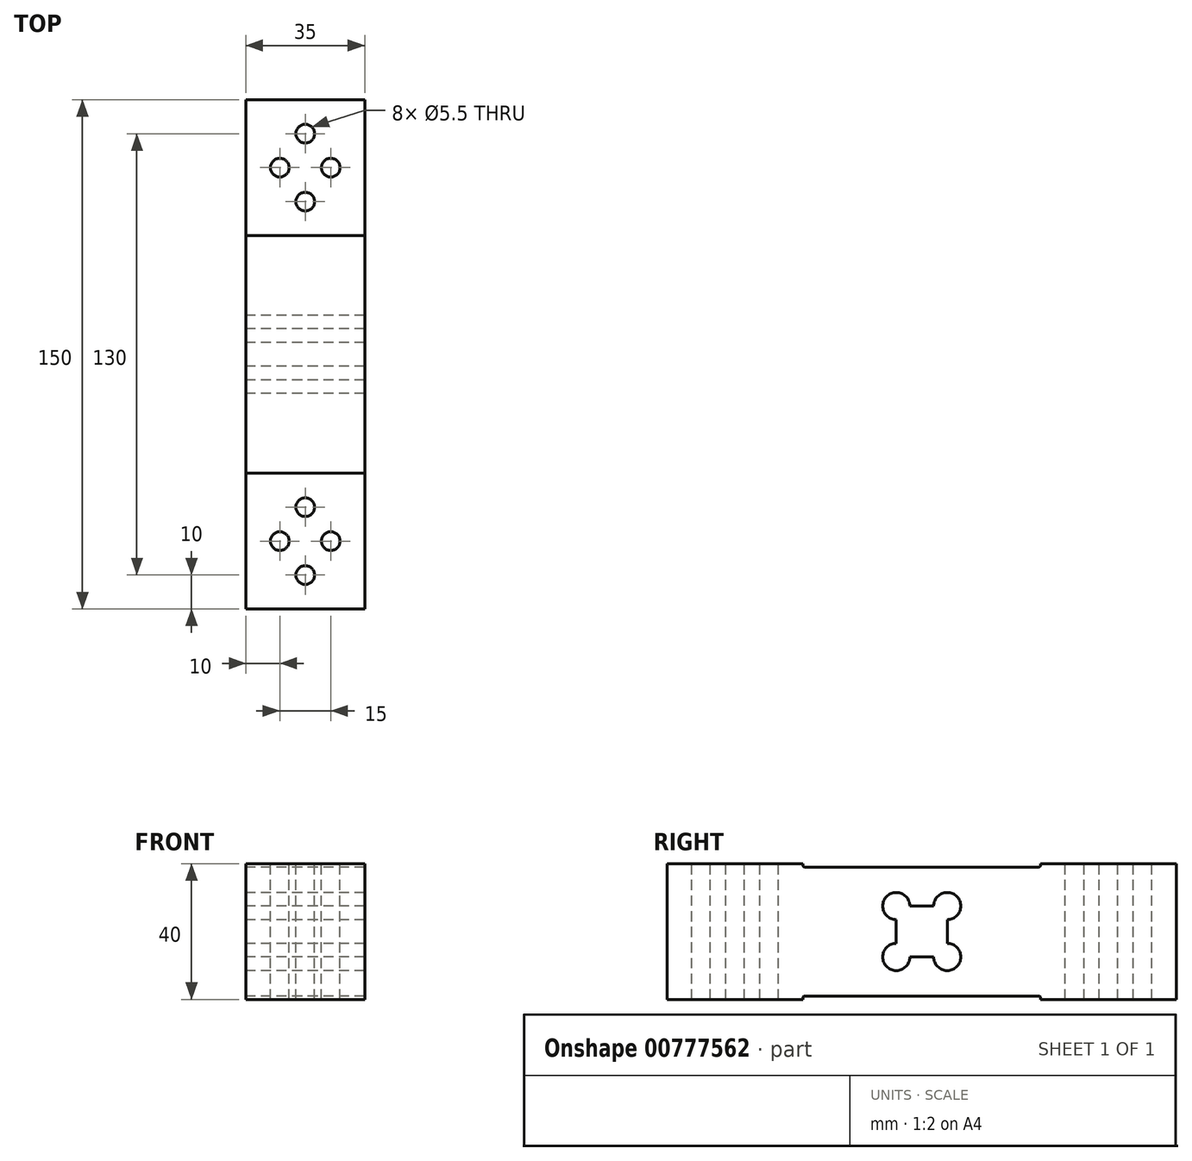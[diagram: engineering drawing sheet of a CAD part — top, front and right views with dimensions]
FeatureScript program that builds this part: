
annotation { "Feature Type Name" : "Feature", "Feature Type Description" : "" }
export const myFeature = defineFeature(function(context is Context, id is Id, definition is map)
    precondition{}
    {
        {
            var Q0;
            Q0=qCreatedBy(makeId("Right.planeOp"),FACE);
            var sketch = newSketch(context, id + "F0", { "sketchPlane" : qUnion([Q0])});
            skLineSegment(sketch, "E0.bottom", {"start": v(0, 0) * mm, "end": v(40, 0) * mm});
            skLineSegment(sketch, "E0.top", {"start": v(0, -40) * mm, "end": v(40, -40) * mm});
            skLineSegment(sketch, "E0.left", {"start": v(0, 0) * mm, "end": v(0, -40) * mm});
            skLineSegment(sketch, "E0.right", {"start": v(150, 0) * mm, "end": v(150, -40) * mm});
            skLineSegment(sketch, "E1.bottom", {"start": v(71.5, -12.5) * mm, "end": v(78.5, -12.5) * mm});
            skLineSegment(sketch, "E1.top", {"start": v(71.5, -27.5) * mm, "end": v(78.5, -27.5) * mm});
            skLineSegment(sketch, "E1.left", {"start": v(67.5, -16.5) * mm, "end": v(67.5, -23.5) * mm});
            skLineSegment(sketch, "E1.right", {"start": v(82.5, -16.5) * mm, "end": v(82.5, -23.5) * mm});
            skPoint(sketch, "E2", {"position": v(75, 0) * mm});
            skPoint(sketch, "E3", {"position": v(75, -12.5) * mm});
            skPoint(sketch, "E4", {"position": v(0, -20) * mm});
            skPoint(sketch, "E5", {"position": v(67.5, -20) * mm});
            skArc(sketch, "E6", {"start": v(78.5, -27.5) * mm, "mid": v(85.33, -30.33) * mm, "end": v(82.5, -23.5) * mm});
            skArc(sketch, "E7", {"start": v(67.5, -23.5) * mm, "mid": v(64.67, -30.33) * mm, "end": v(71.5, -27.5) * mm});
            skArc(sketch, "E8", {"start": v(71.5, -12.5) * mm, "mid": v(64.67, -9.67) * mm, "end": v(67.5, -16.5) * mm});
            skArc(sketch, "E9", {"start": v(82.5, -16.5) * mm, "mid": v(85.33, -9.67) * mm, "end": v(78.5, -12.5) * mm});
            skLineSegment(sketch, "E10", {"start": v(109.5, -1) * mm, "end": v(40.5, -1) * mm});
            skLineSegment(sketch, "E11", {"start": v(109.5, -39) * mm, "end": v(40.5, -39) * mm});
            skLineSegment(sketch, "E12", {"start": v(110, -0.5) * mm, "end": v(110, 0) * mm});
            skLineSegment(sketch, "E13", {"start": v(40, -0.5) * mm, "end": v(40, 0) * mm});
            skLineSegment(sketch, "E14", {"start": v(40, -39.5) * mm, "end": v(40, -40) * mm});
            skLineSegment(sketch, "E15", {"start": v(110, -39.5) * mm, "end": v(110, -40) * mm});
            skPoint(sketch, "E16.visualSharp", {"position": v(110, -39) * mm});
            skArc(sketch, "E16.filletArc", {"start": v(110, -39.5) * mm, "mid": v(109.85, -39.15) * mm, "end": v(109.5, -39) * mm});
            skPoint(sketch, "E17.visualSharp", {"position": v(40, -39) * mm});
            skArc(sketch, "E17.filletArc", {"start": v(40.5, -39) * mm, "mid": v(40.15, -39.15) * mm, "end": v(40, -39.5) * mm});
            skPoint(sketch, "E18.visualSharp", {"position": v(40, -1) * mm});
            skArc(sketch, "E18.filletArc", {"start": v(40, -0.5) * mm, "mid": v(40.15, -0.85) * mm, "end": v(40.5, -1) * mm});
            skPoint(sketch, "E19.visualSharp", {"position": v(110, -1) * mm});
            skArc(sketch, "E19.filletArc", {"start": v(109.5, -1) * mm, "mid": v(109.85, -0.85) * mm, "end": v(110, -0.5) * mm});
            skPoint(sketch, "E20", {"position": v(75, -1) * mm});
            skPoint(sketch, "E21", {"position": v(75, -39) * mm});
            skLineSegment(sketch, "E22.trimOffspring", {"start": v(110, 0) * mm, "end": v(150, 0) * mm});
            skLineSegment(sketch, "E23.trimOffspring", {"start": v(110, -40) * mm, "end": v(150, -40) * mm});
            skSolve(sketch);
        }
        {
            var Q0;
            Q0=makeQuery(id+"F0.imprint","IMPRINT",FACE,{"disambiguationData":[TD([[makeQuery(id+"F0.imprint","IMPRINT",EDGE,{"derivedFrom":sQuery(id+"F0.wireOp",EDGE,"E0.bottom")}),-1.0]])]});
            extrude(context, id + "F1", {"entities" : qUnion([Q0]), "depth" : 35 * mm, "offsetDistance" : 25 * mm});
        }
        {
            var Q0;
            Q0=makeQuery(id+"F1.opExtrude","SWEPT_FACE",FACE,{"disambiguationData":[OSD([sQuery(id+"F0.wireOp",EDGE,"E0.bottom")])]});
            var sketch = newSketch(context, id + "F2", { "sketchPlane" : qUnion([Q0])});
            skCircle(sketch, "E24", {"center": v(17.5, 10) * mm, "radius": 2.75 * mm});
            skCircle(sketch, "E25", {"center": v(17.5, 30) * mm, "radius": 2.75 * mm});
            skCircle(sketch, "E26", {"center": v(25, 20) * mm, "radius": 2.75 * mm});
            skCircle(sketch, "E27", {"center": v(10, 20) * mm, "radius": 2.75 * mm});
            skPoint(sketch, "E28", {"position": v(17.5, 0) * mm});
            skCircle(sketch, "E29", {"center": v(17.5, 120) * mm, "radius": 2.75 * mm});
            skCircle(sketch, "E30", {"center": v(17.5, 140) * mm, "radius": 2.75 * mm});
            skCircle(sketch, "E31", {"center": v(25, 130) * mm, "radius": 2.75 * mm});
            skCircle(sketch, "E32", {"center": v(10, 130) * mm, "radius": 2.75 * mm});
            skSolve(sketch);
        }
        {
            var Q0;
            Q0 = qSketchRegion(id + "F2", true);
            var Q1;
            Q1=makeQuery(id+"F1.opExtrude","SWEPT_FACE",FACE,{"disambiguationData":[OSD([sQuery(id+"F0.wireOp",EDGE,"E0.top")])]});
            extrude(context, id + "F3", {"entities" : qUnion([Q0]), "operationType" : NewBodyOperationType.REMOVE, "endBound" : BoundingType.UP_TO_SURFACE, "oppositeDirection" : true, "depth" : 25 * mm, "endBoundEntityFace" : qUnion([Q1]), "offsetDistance" : 25 * mm});
        }
    });
